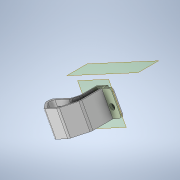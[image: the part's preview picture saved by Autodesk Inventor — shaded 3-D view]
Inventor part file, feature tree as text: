
AUTODESK INVENTOR PART (.ipt)
format: ipt  version: 2022 (Build 260153000, 153)  size: 333,824 bytes
history: native  units: in
note: dims shown in document units (in); Inventor stores cm internally (conversion verified against a paired STEP export)
features: other x9, extrude x7, sketch x7, reference x7, projected_geometry x3, plane x2, fillet x1
ambient origin geometry x8: Origin, YZ Plane, XZ Plane, XY Plane, X Axis, Y Axis, Z Axis, Center Point
bodies: Solid1 (feature_tree)
feature tree (36):
  plane  "Work Plane1"
  extrude  "Extrusion1"  Depth=0.5512in TaperAngle=0.0deg
  extrude  "Extrusion2"  TaperAngle=135.0deg  [1 undecoded]
  extrude  "Extrusion3"  Depth=0.2362in
  extrude  "Extrusion8"  Depth=0.2362in
  extrude  "Extrusion9"  Depth=0.5512in TaperAngle=0.0deg
  plane  "Arbeitsebene3"
  extrude  "Extrusion13"  Depth=0.0591in
  fillet  "Rundung1"  Radius=1.0236in
  extrude  "Extrusion14"  TaperAngle=0.0deg  [1 undecoded]
  sketch  "Sketch1"  dims[d0=0.0591in d1=0.0in d3=0.5512in d4=0.0in]
  sketch  "Sketch2"  dims[d12=0.0591in d13=0.0in d25=135.0deg]
  sketch  "Sketch3"  dims[d26=0.1575in d27=0.2362in]
  reference  "Reference1"
  projected_geometry  "Projected Loop5"
  projected_geometry  "Projected Loop6"
  sketch  "Sketch8"  dims[d28=0.0854in d29=0.2362in]
  reference  "Reference2"
  reference  "Reference3"
  sketch  "Sketch9"  dims[d31=0.4724in d35=0.5512in d36=0.0in]
  reference  "Reference4"
  sketch  "Skizze13"  dims[d40=0.1181in d41=0.0591in d42=1.0236in]
  reference  "Referenz5"
  reference  "Referenz6"
  reference  "Referenz7"
  sketch  "Skizze14"  dims[d43=0.5512in d44=-0.0687in d45=0.0in d50=0.315in d58=0.2559in d60=0.0591in d61=0.0in d62=0.0in d63=0.0591in d64=0.0787in d65=-0.1575in d66=0.1378in d67=0.3937in d68=0.0in]
  projected_geometry  "Projizierte Kontur10"
  other  "Matchboxscope_v1.iam"
  other  "Matchboxscope_sample_v1:1"
  other  "<userpath>\Documents\Matchboxscope\INVENTOR\Matchboxscope_v0.iam"
  other  "Matchboxscope_v0.iam"
  other  "Matchboxscope_sample_v0:1"
  other  "Matchboxscope_middle2_v1:1"
  other  "00_ESP3-CAM:5"
  other  "Bauteil50"
  other  "DIN 912 - ersetzt durch DIN EN ISO 4762 M3 x 25:1"
note: 2 required parameter values undecoded (feature->parameter linkage not recoverable at this tier; creation-order binding heuristic only, values carry confidence <= 0.55)
